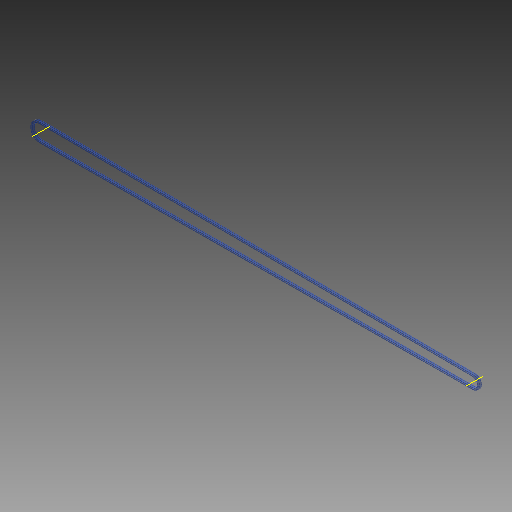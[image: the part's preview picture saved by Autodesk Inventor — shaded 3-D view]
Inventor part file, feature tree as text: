
AUTODESK INVENTOR PART (.ipt)
format: ipt  version: 2017 (Build 210142000, 142)  size: 138,240 bytes
history: native  units: mm
features: other x5, plane x2, pattern_linear x1
ambient origin geometry x8: Origin, YZ Plane, XZ Plane, XY Plane, X Axis, Y Axis, Z Axis, Center Point
bodies: Solid1 (feature_tree), Solid (feature_tree)
feature tree (8):
  other  "Work Axis1"
  other  "Work Axis2"
  plane  "Work Plane2"
  plane  "Work Plane3"
  other  "Path"
  other  "Section Plane"
  pattern_linear  "Strand Pattern"  Spacing1=0.0mm  [1 undecoded]
  other  "Section Sketch"
note: 1 required parameter value undecoded (feature->parameter linkage not recoverable at this tier; creation-order binding heuristic only, values carry confidence <= 0.55)
